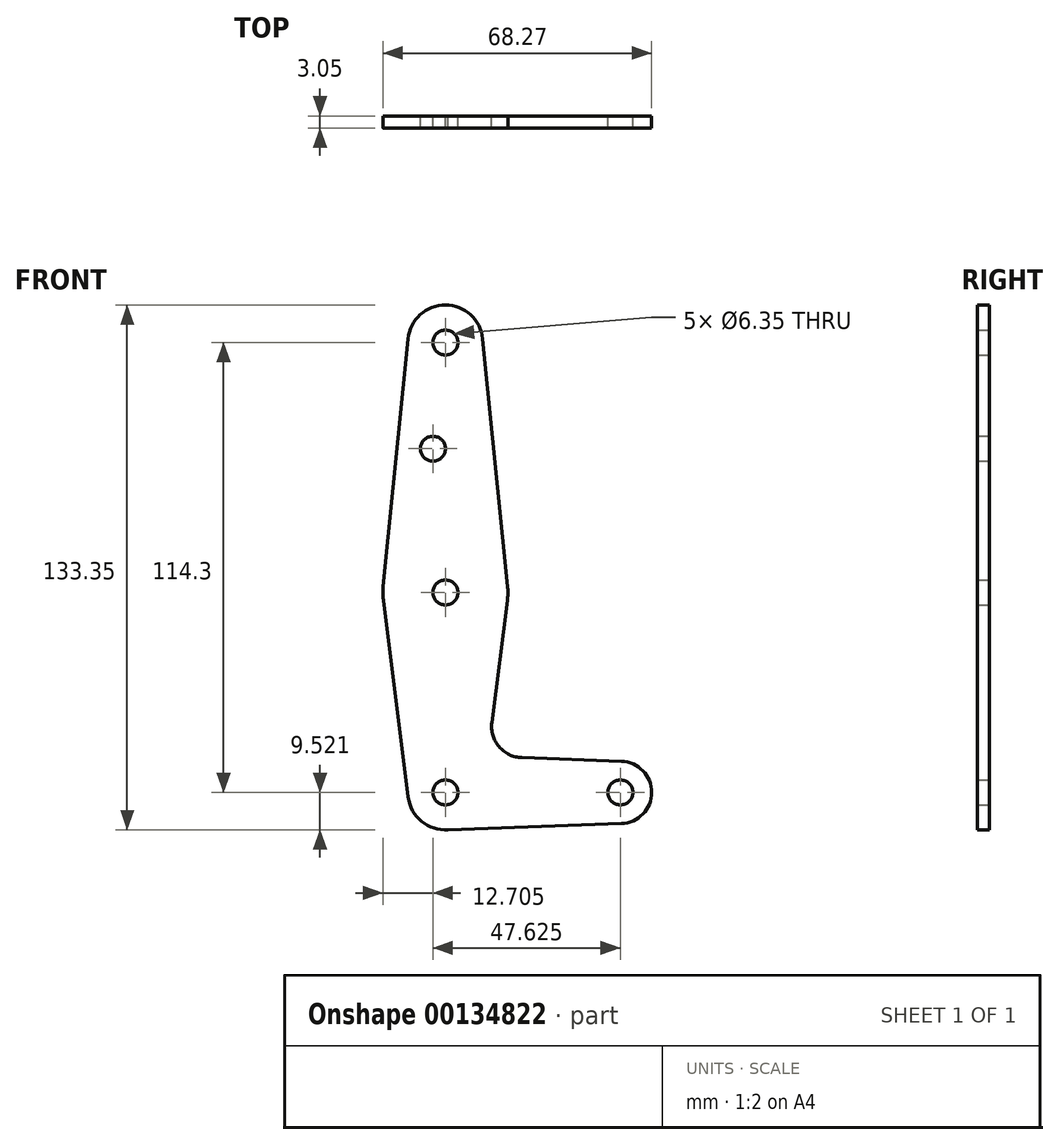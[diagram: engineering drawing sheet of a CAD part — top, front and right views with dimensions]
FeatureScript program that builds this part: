
annotation { "Feature Type Name" : "Feature", "Feature Type Description" : "" }
export const myFeature = defineFeature(function(context is Context, id is Id, definition is map)
    precondition{}
    {
        {
            var Q0;
            Q0=qCreatedBy(makeId("Front.planeOp"),FACE);
            var sketch = newSketch(context, id + "F0", { "sketchPlane" : qUnion([Q0])});
            skLineSegment(sketch, "E0", {"start": v(0, 74.82) * mm, "end": v(0, -39.48) * mm, "construction": true});
            skLineSegment(sketch, "E1", {"start": v(0, -39.48) * mm, "end": v(44.45, -39.48) * mm});
            skCircle(sketch, "E2", {"center": v(0, 74.82) * mm, "radius": 9.53 * mm});
            skCircle(sketch, "E3", {"center": v(0, 11.32) * mm, "radius": 15.88 * mm});
            skCircle(sketch, "E4", {"center": v(0, -39.48) * mm, "radius": 9.53 * mm});
            skCircle(sketch, "E5", {"center": v(44.45, -39.48) * mm, "radius": 7.94 * mm});
            skLineSegment(sketch, "E6", {"start": v(-9.48, 75.77) * mm, "end": v(-15.8, 12.9) * mm});
            skLineSegment(sketch, "E7", {"start": v(9.48, 75.77) * mm, "end": v(15.8, 12.9) * mm});
            skLineSegment(sketch, "E8", {"start": v(19.4, -30.64) * mm, "end": v(44.73, -31.55) * mm});
            skLineSegment(sketch, "E9", {"start": v(0, -49) * mm, "end": v(44.73, -47.41) * mm});
            skLineSegment(sketch, "E10", {"start": v(-15.75, 9.34) * mm, "end": v(-9.45, -40.67) * mm});
            skLineSegment(sketch, "E11", {"start": v(11.8, -21.7) * mm, "end": v(15.75, 9.31) * mm});
            skCircle(sketch, "E12", {"center": v(0, 74.82) * mm, "radius": 3.18 * mm});
            skCircle(sketch, "E13", {"center": v(-3.17, 47.85) * mm, "radius": 3.18 * mm});
            skCircle(sketch, "E14", {"center": v(0, 11.32) * mm, "radius": 3.18 * mm});
            skCircle(sketch, "E15", {"center": v(44.45, -39.48) * mm, "radius": 3.18 * mm});
            skCircle(sketch, "E16", {"center": v(0, -39.48) * mm, "radius": 3.18 * mm});
            skArc(sketch, "E17.filletArc", {"start": v(11.8, -21.7) * mm, "mid": v(13.62, -27.85) * mm, "end": v(19.4, -30.64) * mm});
            skSolve(sketch);
        }
        {
            var Q0;
            Q0 = qSketchRegion(id + "F0", true);
            extrude(context, id + "F1", {"entities" : qUnion([Q0]), "depth" : 3.05 * mm});
        }
    });
